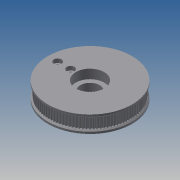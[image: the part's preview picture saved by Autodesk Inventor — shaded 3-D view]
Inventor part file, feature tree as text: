
AUTODESK INVENTOR PART (.ipt)
format: ipt  version: 2013 (Build 170138000, 138)  size: 1,209,344 bytes
history: native  units: mm
features: extrude x5, sketch x5, pattern_circular x1, chamfer x1, mirror x1
ambient origin geometry x8: Origin, YZ Plane, XZ Plane, XY Plane, X Axis, Y Axis, Z Axis, Center Point
bodies: Solid1 (feature_tree)
feature tree (13):
  extrude  "Extrusion1"  Depth=0.628319mm
  pattern_circular  "Circular Pattern1"  [2 undecoded]
  extrude  "Extrusion3"  Depth=0.75mm
  chamfer  "Chamfer2"  Distance=0.254mm
  mirror  "Mirror1"
  extrude  "Extrusion4"  Depth=8.0mm TaperAngle=0.0deg
  extrude  "Extrusion5"  Depth=1000.0mm
  extrude  "Extrusion6"  TaperAngle=360.0deg  [1 undecoded]
  sketch  "Sketch1"  dims[d0=63.661977mm d9=0.628319mm]
  sketch  "Sketch3"  dims[d11=0.254mm]
  sketch  "Sketch4"  dims[d12=0.3mm]
  sketch  "Sketch5"  dims[d13=0.4mm]
  sketch  "Sketch6"  dims[d14=1.0mm d15=0.555mm d16=0.75mm d17=0.254mm d18=8.0mm d19=0.0mm d20=1000.0mm d21=360.0deg d23=0.1mm d32=2.5mm d33=0.0mm d34=1.0mm d35=2.0mm d36=45.0deg d37=15.0mm d39=3.5mm d40=15.0mm d41=25.0mm d42=2.0mm d43=0.0mm d44=6.0mm d46=3.0mm d47=0.0mm d49=22.0mm d51=7.0mm d52=0.0mm d53=1.0mm]
note: 3 required parameter values undecoded (feature->parameter linkage not recoverable at this tier; creation-order binding heuristic only, values carry confidence <= 0.55)
